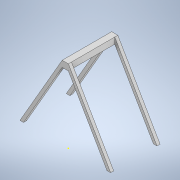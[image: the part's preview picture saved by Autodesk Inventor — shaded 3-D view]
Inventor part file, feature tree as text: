
AUTODESK INVENTOR PART (.ipt)
format: ipt  version: 2022 (Build 260153000, 153)  size: 143,872 bytes
history: native  units: mm
features: sketch x8, extrude x6
ambient origin geometry x8: Origin, YZ Plane, XZ Plane, XY Plane, X Axis, Y Axis, Z Axis, Center Point
bodies: Solid1 (feature_tree)
feature tree (14):
  sketch  "Sketch1"  dims[d0=650.0mm d3=30.0mm d4=0.0mm]
  extrude  "Extrusion1"  Depth=30.0mm TaperAngle=0.0deg
  extrude  "Extrusion2"  Depth=60.0mm
  extrude  "Extrusion3"  Depth=60.0mm TaperAngle=0.0deg
  sketch  "Sketch5"  dims[d16=30.0mm d17=0.0mm]
  extrude  "Extrusion4"  Depth=30.0mm TaperAngle=0.0deg
  extrude  "Extrusion5"  [1 undecoded]
  extrude  "Extrusion6"  [1 undecoded]
  sketch  "Sketch2"  dims[d5=60.0mm d6=750.555mm]
  sketch  "Sketch3"  dims[d8=30.0mm d9=0.0mm d10=60.0mm d11=0.0mm]
  sketch  "Sketch4"  dims[d12=420.0mm d13=0.0mm d14=30.0mm d15=0.0mm]
  sketch  "Sketch6"
  sketch  "Sketch7"
  sketch  "Sketch8"
note: 2 required parameter values undecoded (feature->parameter linkage not recoverable at this tier; creation-order binding heuristic only, values carry confidence <= 0.55)
